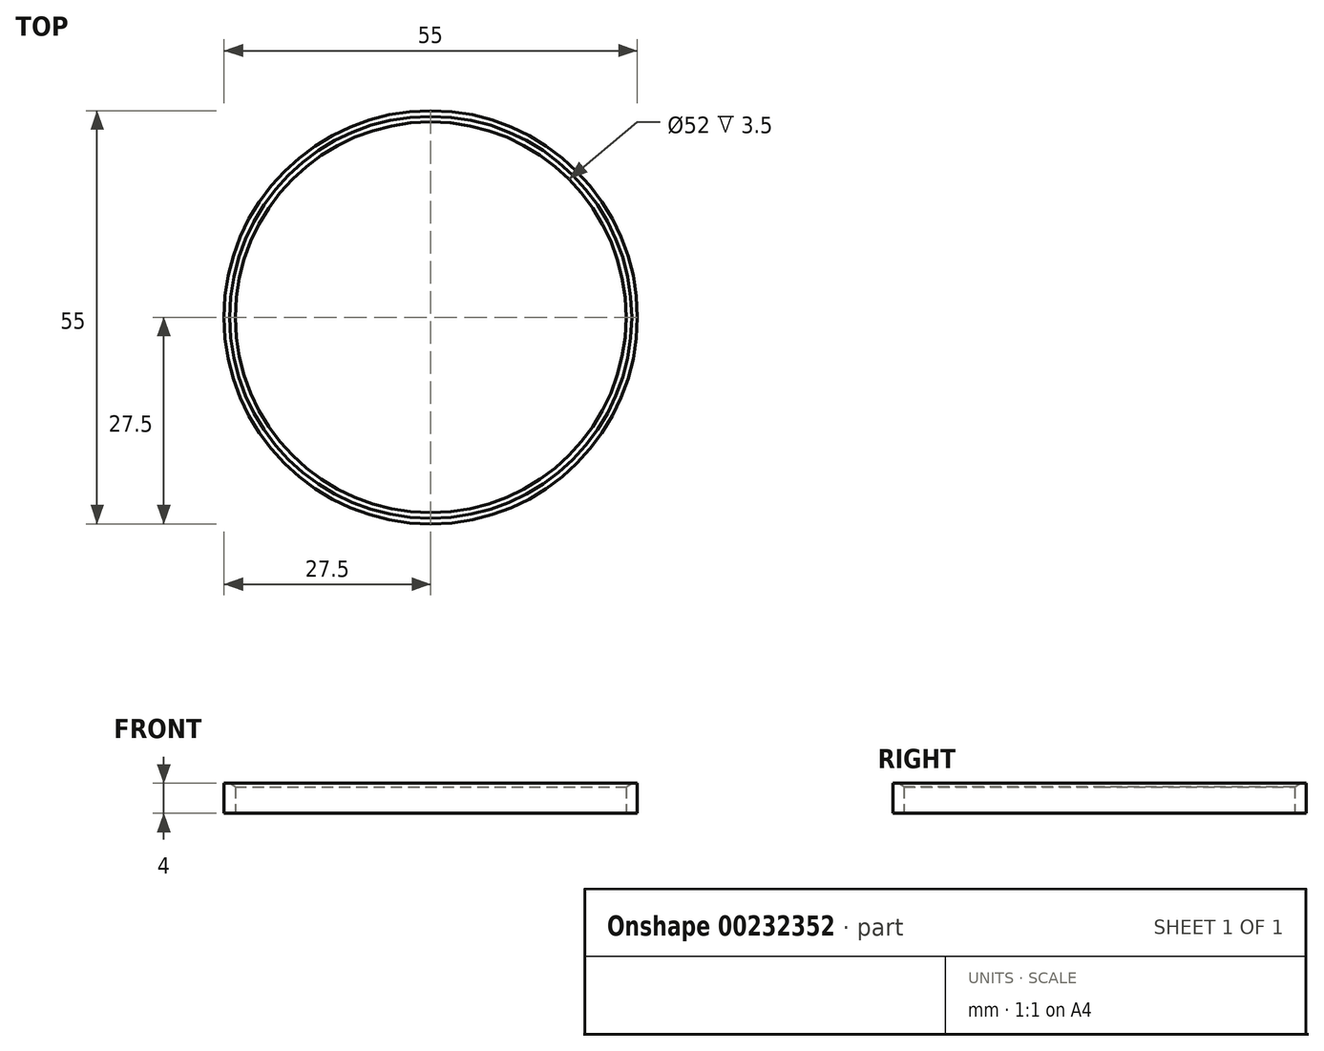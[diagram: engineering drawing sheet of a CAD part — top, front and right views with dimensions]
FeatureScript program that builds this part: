
annotation { "Feature Type Name" : "Feature", "Feature Type Description" : "" }
export const myFeature = defineFeature(function(context is Context, id is Id, definition is map)
    precondition{}
    {
        {
            var Q0;
            Q0=qCreatedBy(makeId("Front.planeOp"),FACE);
            var sketch = newSketch(context, id + "F0", { "sketchPlane" : qUnion([Q0])});
            skLineSegment(sketch, "E0", {"start": v(0, 0) * mm, "end": v(0, 17.75) * mm, "construction": true});
            skLineSegment(sketch, "E1.bottom", {"start": v(26, 0) * mm, "end": v(27.5, 0) * mm});
            skLineSegment(sketch, "E1.top", {"start": v(26.75, 4) * mm, "end": v(27.5, 4) * mm});
            skLineSegment(sketch, "E1.left", {"start": v(26, 0) * mm, "end": v(26, 3.5) * mm});
            skLineSegment(sketch, "E1.right", {"start": v(27.5, 0) * mm, "end": v(27.5, 4) * mm});
            skLineSegment(sketch, "E2", {"start": v(26, 3.5) * mm, "end": v(26.75, 4) * mm});
            skPoint(sketch, "E3.orphan", {"position": v(26, 4) * mm});
            skSolve(sketch);
        }
        {
            var Q0;
            Q0=makeQuery(id+"F0.imprint","IMPRINT",FACE,{"disambiguationData":[TD([[makeQuery(id+"F0.imprint","IMPRINT",EDGE,{"derivedFrom":sQuery(id+"F0.wireOp",EDGE,"E1.bottom")}),1.0]])]});
            var Q1;
            Q1=sQuery(id+"F0.wireOp",EDGE,"E0");
            revolve(context, id + "F1", {"entities" : qUnion([Q0]), "axis" : qUnion([Q1]), "revolveType" : RevolveType.FULL});
        }
    });
